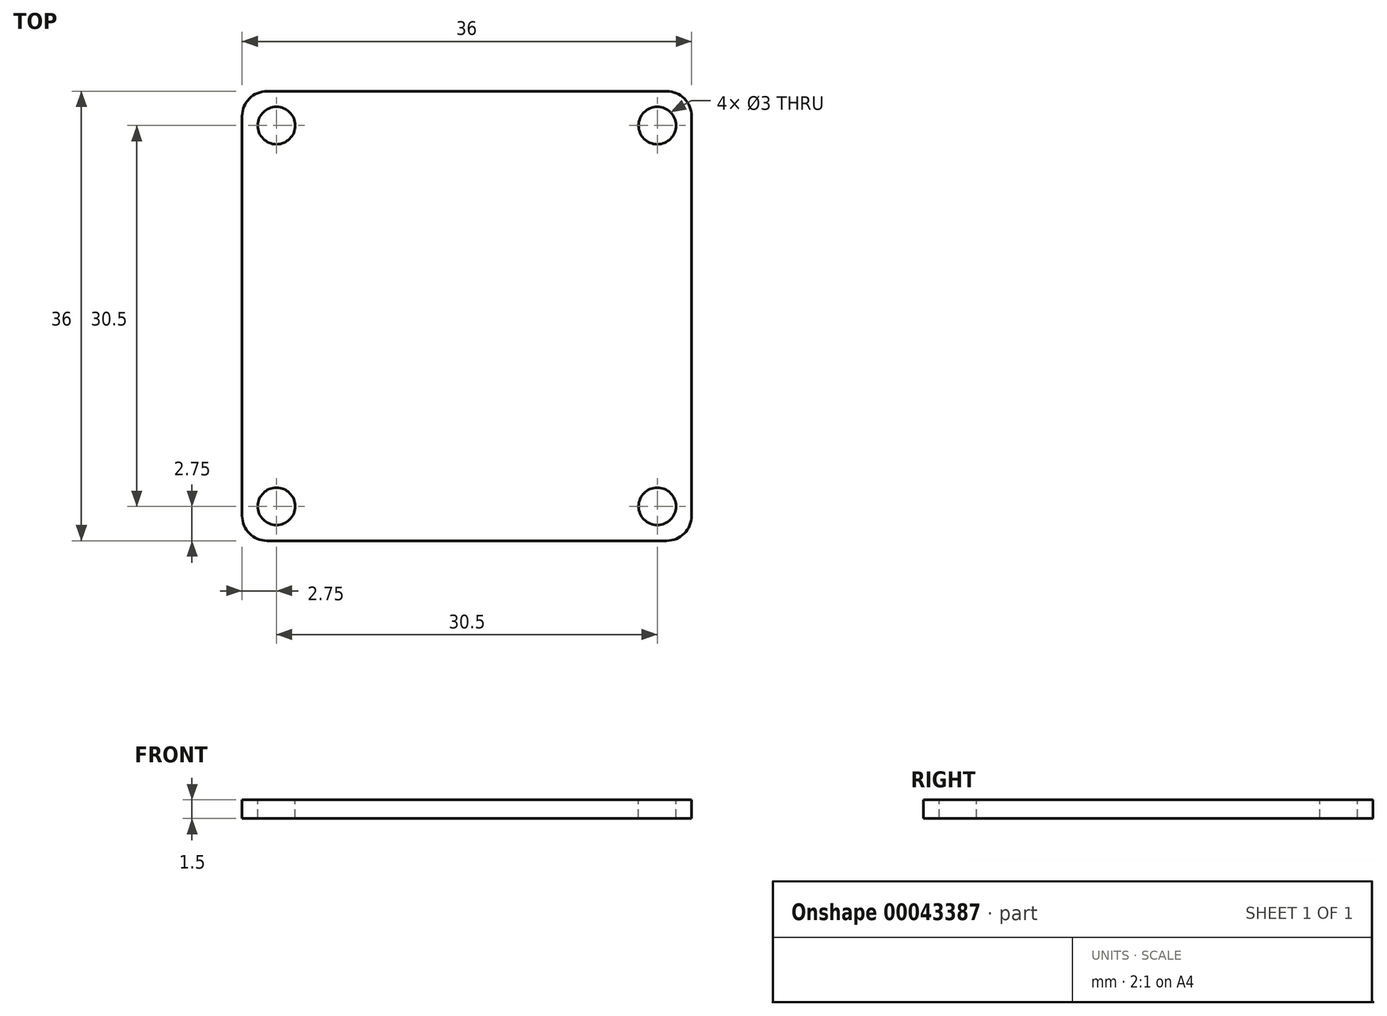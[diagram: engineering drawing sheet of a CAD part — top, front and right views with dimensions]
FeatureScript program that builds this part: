
annotation { "Feature Type Name" : "Feature", "Feature Type Description" : "" }
export const myFeature = defineFeature(function(context is Context, id is Id, definition is map)
    precondition{}
    {
        {
            var Q0;
            Q0=qCreatedBy(makeId("Top.planeOp"),FACE);
            var sketch = newSketch(context, id + "F0", { "sketchPlane" : qUnion([Q0])});
            skLineSegment(sketch, "E0.bottom", {"start": v(-16, 18) * mm, "end": v(16, 18) * mm});
            skLineSegment(sketch, "E0.top", {"start": v(-16, -18) * mm, "end": v(16, -18) * mm});
            skLineSegment(sketch, "E0.left", {"start": v(-18, 16) * mm, "end": v(-18, -16) * mm});
            skLineSegment(sketch, "E0.right", {"start": v(18, 16) * mm, "end": v(18, -16) * mm});
            skPoint(sketch, "E1", {"position": v(0, 18) * mm});
            skPoint(sketch, "E2", {"position": v(18, 0) * mm});
            skPoint(sketch, "E3.visualSharp", {"position": v(-18, 18) * mm});
            skArc(sketch, "E3.filletArc", {"start": v(-16, 18) * mm, "mid": v(-17.41, 17.41) * mm, "end": v(-18, 16) * mm});
            skPoint(sketch, "E4.visualSharp", {"position": v(18, 18) * mm});
            skArc(sketch, "E4.filletArc", {"start": v(18, 16) * mm, "mid": v(17.41, 17.41) * mm, "end": v(16, 18) * mm});
            skPoint(sketch, "E5.visualSharp", {"position": v(18, -18) * mm});
            skArc(sketch, "E5.filletArc", {"start": v(16, -18) * mm, "mid": v(17.41, -17.41) * mm, "end": v(18, -16) * mm});
            skPoint(sketch, "E6.visualSharp", {"position": v(-18, -18) * mm});
            skArc(sketch, "E6.filletArc", {"start": v(-18, -16) * mm, "mid": v(-17.41, -17.41) * mm, "end": v(-16, -18) * mm});
            skLineSegment(sketch, "E7", {"start": v(-15.25, 15.25) * mm, "end": v(-15.25, -15.25) * mm, "construction": true});
            skLineSegment(sketch, "E8", {"start": v(15.25, 15.25) * mm, "end": v(15.25, -15.25) * mm, "construction": true});
            skPoint(sketch, "E9", {"position": v(-15.25, 0) * mm});
            skPoint(sketch, "E10", {"position": v(15.25, 0) * mm});
            skSolve(sketch);
        }
        {
            var Q0;
            Q0 = qSketchRegion(id + "F0", true);
            extrude(context, id + "F1", {"entities" : qUnion([Q0]), "oppositeDirection" : true, "depth" : 1.5 * mm});
        }
        {
            var Q0;
            Q0=sQuery(id+"F0.wireOp",VERTEX,"E7.start");
            var Q1;
            Q1=sQuery(id+"F0.wireOp",VERTEX,"E7.end");
            var Q2;
            Q2=sQuery(id+"F0.wireOp",VERTEX,"E8.start");
            var Q3;
            Q3=sQuery(id+"F0.wireOp",VERTEX,"E8.end");
            var Q4;
            Q4=makeQuery(id+"F1.opExtrude","SWEPT_BODY",BODY,{"disambiguationData":[OSD([sQuery(id+"F0.wireOp",EDGE,"E0.bottom"),sQuery(id+"F0.wireOp",EDGE,"E0.top"),sQuery(id+"F0.wireOp",EDGE,"E0.left"),sQuery(id+"F0.wireOp",EDGE,"E0.right"),sQuery(id+"F0.wireOp",EDGE,"E3.filletArc"),sQuery(id+"F0.wireOp",EDGE,"E4.filletArc"),sQuery(id+"F0.wireOp",EDGE,"E5.filletArc"),sQuery(id+"F0.wireOp",EDGE,"E6.filletArc")])]});
            hole(context, id + "F2", {"style" : HoleStyle.SIMPLE, "holeDiameter" : 3 * mm, "endStyle" : HoleEndStyle.THROUGH, "locations" : qUnion([Q0, Q1, Q2, Q3]), "scope" : qUnion([Q4])});
        }
    });
